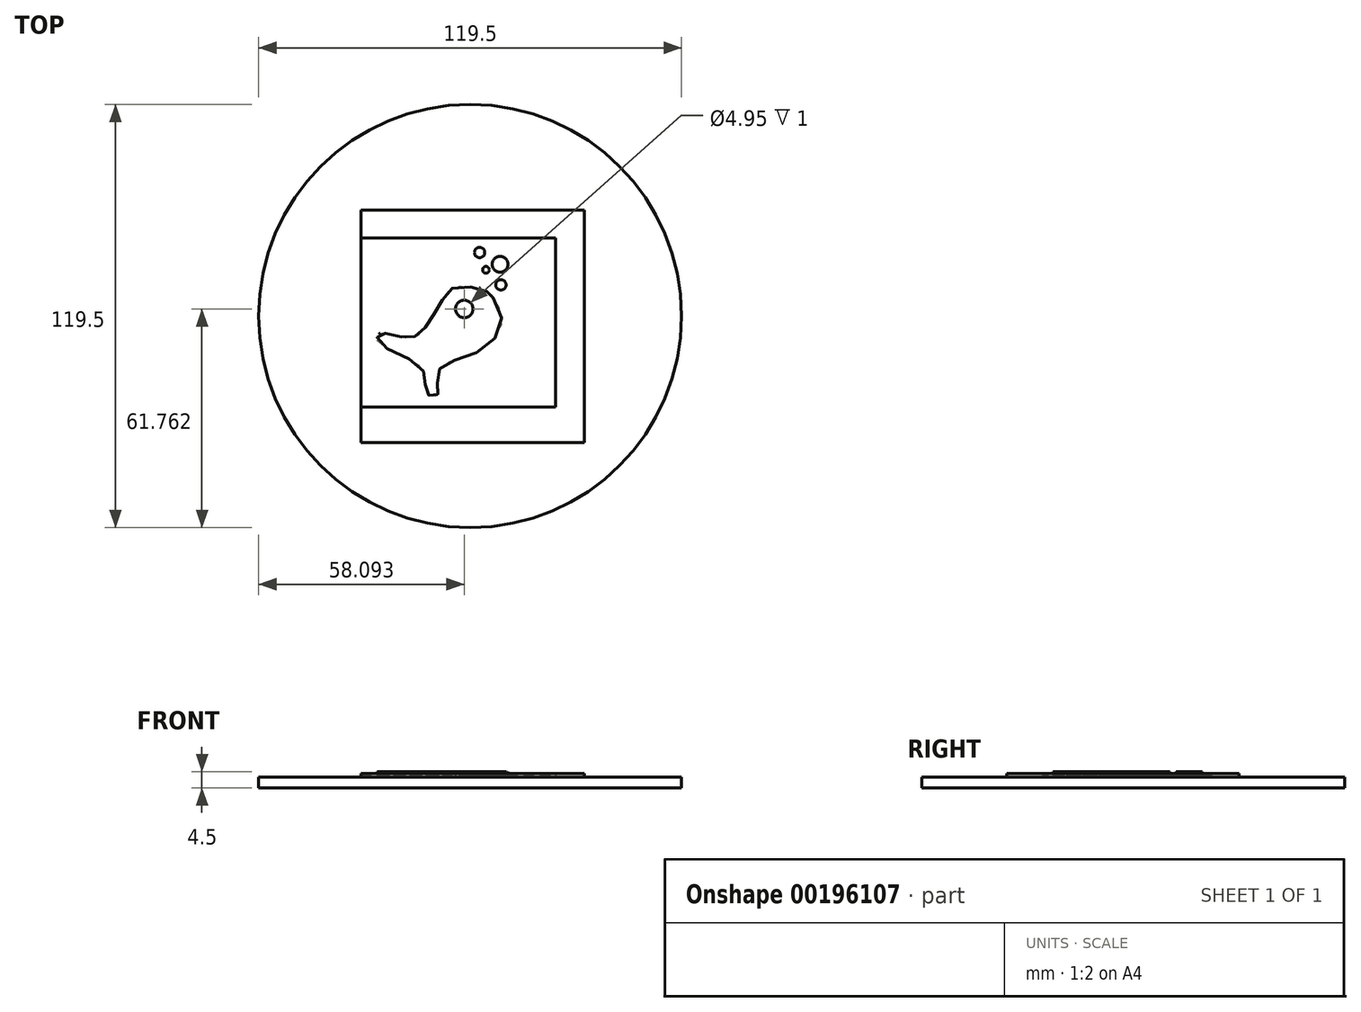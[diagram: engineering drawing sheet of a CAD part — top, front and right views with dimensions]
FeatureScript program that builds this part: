
annotation { "Feature Type Name" : "Feature", "Feature Type Description" : "" }
export const myFeature = defineFeature(function(context is Context, id is Id, definition is map)
    precondition{}
    {
        {
            var Q0;
            Q0=qCreatedBy(makeId("Top.planeOp"),FACE);
            var sketch = newSketch(context, id + "F0", { "sketchPlane" : qUnion([Q0])});
            skCircle(sketch, "E0", {"center": v(0, 0) * mm, "radius": 59.75 * mm});
            skSolve(sketch);
        }
        {
            var Q0;
            Q0=makeQuery(id+"F0.imprint","IMPRINT",FACE,{"disambiguationData":[TD([[makeQuery(id+"F0.imprint","IMPRINT",EDGE,{"derivedFrom":sQuery(id+"F0.wireOp",EDGE,"E0")}),1.0]])]});
            extrude(context, id + "F1", {"entities" : qUnion([Q0]), "depth" : 3 * mm});
        }
        {
            var Q0;
            Q0=makeQuery(id+"F1.opExtrude","CAP_FACE",FACE,{"disambiguationData":[OSD([sQuery(id+"F0.wireOp",EDGE,"E0")])],"isStart":false});
            var sketch = newSketch(context, id + "F2", { "sketchPlane" : qUnion([Q0])});
            skLineSegment(sketch, "E1.bottom", {"start": v(-30.88, 29.9) * mm, "end": v(32.29, 29.9) * mm});
            skLineSegment(sketch, "E1.top", {"start": v(-30.88, -35.8) * mm, "end": v(32.29, -35.8) * mm});
            skLineSegment(sketch, "E1.left", {"start": v(-30.88, 29.9) * mm, "end": v(-30.88, -35.8) * mm});
            skLineSegment(sketch, "E1.right", {"start": v(32.29, 29.9) * mm, "end": v(32.29, -35.8) * mm});
            skLineSegment(sketch, "E2.bottom", {"start": v(-30.88, 22.04) * mm, "end": v(24.14, 22.04) * mm});
            skLineSegment(sketch, "E2.top", {"start": v(-30.88, -25.69) * mm, "end": v(24.14, -25.69) * mm});
            skLineSegment(sketch, "E2.left", {"start": v(-30.88, 22.04) * mm, "end": v(-30.88, -25.69) * mm});
            skLineSegment(sketch, "E2.right", {"start": v(24.14, 22.04) * mm, "end": v(24.14, -25.69) * mm});
            skSolve(sketch);
        }
        {
            var Q0;
            {var subQ4=sQuery(id+"F2.wireOp",EDGE,"E1.bottom");Q0=makeQuery(id+"F2.imprint","IMPRINT",FACE,{"disambiguationData":[TD([[makeQuery(id+"F2.imprint","IMPRINT",EDGE,{"derivedFrom":subQ4}),-1.0]])]});}
            extrude(context, id + "F3", {"entities" : qUnion([Q0]), "operationType" : NewBodyOperationType.ADD, "depth" : 1 * mm});
        }
        {
            var Q0;
            Q0=makeQuery(id+"F1.opExtrude","CAP_FACE",FACE,{"disambiguationData":[OSD([sQuery(id+"F0.wireOp",EDGE,"E0")])],"isStart":false});
            var sketch = newSketch(context, id + "F4", { "sketchPlane" : qUnion([Q0])});
            skLineSegment(sketch, "E3", {"start": v(-30.88, 22.04) * mm, "end": v(-30.88, -25.69) * mm});
            skSolve(sketch);
        }
        {
            var Q0;
            Q0=makeQuery(id+"F4.imprint","IMPRINT",FACE,{"disambiguationData":[TD([[makeQuery(id+"F4.imprint","IMPRINT",EDGE,{"derivedFrom":sQuery(id+"F4.wireOp",EDGE,"E3")}),1.0]])]});
            extrude(context, id + "F5", {"entities" : qUnion([Q0]), "operationType" : NewBodyOperationType.ADD, "depth" : 0.5 * mm});
        }
        {
            var Q0;
            Q0=makeQuery(id+"F5.opExtrude","CAP_FACE",FACE,{"disambiguationData":[OSD([sQuery(id+"F2.wireOp",EDGE,"E2.bottom"),sQuery(id+"F2.wireOp",EDGE,"E2.top"),sQuery(id+"F2.wireOp",EDGE,"E2.right"),sQuery(id+"F4.wireOp",EDGE,"E3")])],"isStart":false});
            var sketch = newSketch(context, id + "F6", { "sketchPlane" : qUnion([Q0])});
            skFitSpline(sketch, "E4", {"points": [v(-7.9, 4.46) * mm, v(-3.1, 8.47) * mm, v(4.92, 6.91) * mm, v(5.03, 6.91) * mm, v(8.82, 0) * mm, v(2.24, -10.13) * mm, v(-8.23, -14.48) * mm, v(-9.12, -19.83) * mm, v(-9.35, -22.39) * mm, v(-11.8, -22.28) * mm, v(-12.69, -18.93) * mm, v(-14.47, -13.92) * mm, v(-25.72, -7.57) * mm, v(-25.72, -5) * mm, v(-20.26, -5.68) * mm, v(-15.14, -5.56) * mm, v(-11.57, -1.55) * mm, v(-7.9, 4.46) * mm]});
            skSolve(sketch);
        }
        {
            var Q0;
            Q0=makeQuery(id+"F6.imprint","IMPRINT",FACE,{"disambiguationData":[TD([[makeQuery(id+"F6.imprint","IMPRINT",EDGE,{"derivedFrom":sQuery(id+"F6.wireOp",EDGE,"E4")}),-1.0]])]});
            extrude(context, id + "F7", {"entities" : qUnion([Q0]), "operationType" : NewBodyOperationType.ADD, "depth" : 1 * mm});
        }
        {
            var Q0;
            Q0=makeQuery(id+"F7.opExtrude","CAP_FACE",FACE,{"disambiguationData":[OSD([sQuery(id+"F6.wireOp",EDGE,"E4")])],"isStart":false});
            var sketch = newSketch(context, id + "F8", { "sketchPlane" : qUnion([Q0])});
            skCircle(sketch, "E5", {"center": v(-1.66, 2.01) * mm, "radius": 2.47 * mm});
            skSolve(sketch);
        }
        {
            var Q0;
            Q0=makeQuery(id+"F8.imprint","IMPRINT",FACE,{"disambiguationData":[TD([[makeQuery(id+"F8.imprint","IMPRINT",EDGE,{"derivedFrom":sQuery(id+"F8.wireOp",EDGE,"E5")}),1.0]])]});
            extrude(context, id + "F9", {"entities" : qUnion([Q0]), "operationType" : NewBodyOperationType.REMOVE, "oppositeDirection" : true, "depth" : 1 * mm});
        }
        {
            var Q0;
            Q0=makeQuery(id+"F5.opExtrude","CAP_FACE",FACE,{"disambiguationData":[OSD([sQuery(id+"F2.wireOp",EDGE,"E2.bottom"),sQuery(id+"F2.wireOp",EDGE,"E2.top"),sQuery(id+"F2.wireOp",EDGE,"E2.right"),sQuery(id+"F4.wireOp",EDGE,"E3")])],"isStart":false});
            var sketch = newSketch(context, id + "F10", { "sketchPlane" : qUnion([Q0])});
            skCircle(sketch, "E6", {"center": v(8.48, 14.6) * mm, "radius": 2.22 * mm});
            skCircle(sketch, "E7", {"center": v(8.7, 8.8) * mm, "radius": 1.47 * mm});
            skCircle(sketch, "E8", {"center": v(2.69, 17.94) * mm, "radius": 1.47 * mm});
            skCircle(sketch, "E9", {"center": v(4.47, 13.04) * mm, "radius": 0.95 * mm});
            skSolve(sketch);
        }
        {
            var Q0;
            Q0=makeQuery(id+"F10.imprint","IMPRINT",FACE,{"disambiguationData":[TD([[makeQuery(id+"F10.imprint","IMPRINT",EDGE,{"derivedFrom":sQuery(id+"F10.wireOp",EDGE,"E6")}),1.0]])]});
            var Q1;
            Q1=makeQuery(id+"F10.imprint","IMPRINT",FACE,{"disambiguationData":[TD([[makeQuery(id+"F10.imprint","IMPRINT",EDGE,{"derivedFrom":sQuery(id+"F10.wireOp",EDGE,"E8")}),1.0]])]});
            var Q2;
            Q2=makeQuery(id+"F10.imprint","IMPRINT",FACE,{"disambiguationData":[TD([[makeQuery(id+"F10.imprint","IMPRINT",EDGE,{"derivedFrom":sQuery(id+"F10.wireOp",EDGE,"E9")}),1.0]])]});
            var Q3;
            Q3=makeQuery(id+"F10.imprint","IMPRINT",FACE,{"disambiguationData":[TD([[makeQuery(id+"F10.imprint","IMPRINT",EDGE,{"derivedFrom":sQuery(id+"F10.wireOp",EDGE,"E7")}),1.0]])]});
            extrude(context, id + "F11", {"entities" : qUnion([Q0, Q1, Q2, Q3]), "operationType" : NewBodyOperationType.ADD, "depth" : 1 * mm});
        }
    });
